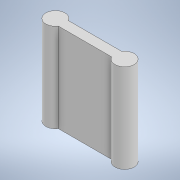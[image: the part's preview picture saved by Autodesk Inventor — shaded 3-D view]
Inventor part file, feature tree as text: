
AUTODESK INVENTOR PART (.ipt)
format: ipt  version: 2020 (Build 240168000, 168)  size: 128,512 bytes
history: native  units: mm
features: extrude x1, sketch x1
ambient origin geometry x8: Origin, YZ Plane, XZ Plane, XY Plane, X Axis, Y Axis, Z Axis, Center Point
bodies: Solid1 (feature_tree)
feature tree (2):
  extrude  "Extrusion1"  Depth=2.2mm
  sketch  "Sketch1"  dims[d0=4.314707mm d2=12.0mm d3=4.315mm d8=2.2mm d9=12.0mm d10=20.0mm d11=0.0mm]
